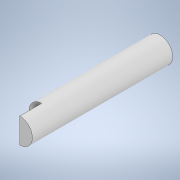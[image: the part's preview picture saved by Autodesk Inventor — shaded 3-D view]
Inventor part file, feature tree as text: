
AUTODESK INVENTOR PART (.ipt)
format: ipt  version: 2022 (Build 260153000, 153)  size: 126,464 bytes
history: mixed  units: mm
features: extrude x4, sketch x4, other x1, imported_body x1
ambient origin geometry x8: Origin, YZ Plane, XZ Plane, XY Plane, X Axis, Y Axis, Z Axis, Center Point
bodies: Solid1 (imported_parasolid)
feature tree (10):
  extrude  "Extrusion1"  Depth=20.4mm TaperAngle=0.0deg
  extrude  "Extrusion2"  Depth=4.325mm TaperAngle=0.0deg
  extrude  "Extrusion3"  [1 undecoded]
  extrude  "Extrusion4"  [1 undecoded]
  sketch  "Sketch1"  dims[d0=254.0mm d1=0.0mm d2=20.4mm d3=0.0mm]
  sketch  "Sketch2"  dims[d4=2.5mm d5=0.0mm d6=4.325mm d7=0.0mm]
  sketch  "Sketch3"
  sketch  "Sketch4"
  other  "Boss-Extrude1"
  imported_body  NMx_Import_Brep_tag  [imported B-rep: ~5 faces, bbox_mm=[2.5, 5.0, 27.9]]
note: 2 required parameter values undecoded (feature->parameter linkage not recoverable at this tier; creation-order binding heuristic only, values carry confidence <= 0.55)
